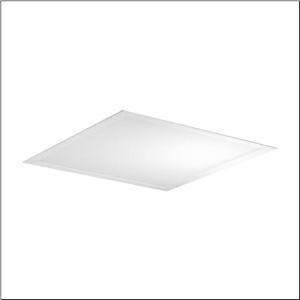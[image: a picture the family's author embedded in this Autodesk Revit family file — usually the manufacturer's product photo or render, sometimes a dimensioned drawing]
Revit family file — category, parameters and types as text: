
# Revit family: apollon_r__21_square_51mq11wd2454_78a7
name_source: partatom
category: Lighting Fixtures
units: mm (PartAtom-declared; Revit-internal decimal feet)

## family parameters
Cut with Voids When Loaded = No
Host = Face
Light Source = No
Part Type = Normal
Room Calculation Point = No
Round Connector Dimension = Use Diameter
Shared = No

## types (1)
- Apollon® 21 square (1 x LED, 4200 lm, 24.7 W, 4000K)
    Apparent Load = 25 VA
    CIE Flux Codes = 60 87 97 100 100
    Color Rendering = 80
    Color Temperature = 4000K
    Default Elevation = 1800 mm
    Description = Apollon® 21 square, office luminaire, primary optical cover: micro prismatic cover, of PMMA, CAT 2 (L<= 3000cd/m²), light emission: direct distribution, primary light characteristic: symmetric, installation type: lay-in mounting, LED, rated luminous flux: 4.200lm, luminous efficacy: 170lm/W, light colour: 840, colour temperature: 4000K, with terminal, 5-pole, mains connection: 220..240V, AC/DC, 0/50..60Hz, rated input power: 24.7W, housing, of aluminium, coated, traffic white (RAL 9016), module: M625, length: 620mm, width: 620mm, height: 30mm, housing upper side, of sheet steel, galvanised, protection rating (complete): IP20, protection rating (lamp compartment, on room side): IP54, insulation class (complete): insulation class II (safety insulation), certification: CE, ENEC, impact resistance: IK03, permissible operating ambient temperature: -20..+45°C, permissible storage temperature: -40..+80°C, packaging unit: 1 piece
    Height = 0 mm  [stored 0 ft]
    Lamp = 1 x LED
    Lamp Light Flux = 4200 lm
    Lamp Power = 24.7 W
    Lamp count = 1
    Length = 620 mm
    Luminous efficacy = 170 lm/W
    Manufacturer = Siteco
    ModVariant = No
    Model = 51MQ11WD2454
    Mounting Place = Ceiling
    Mounting Type = Recessed
    Number of Poles = 1
    OnlyDefault = Yes
    Power Factor = 1
    Product Name = Apollon® 21 square
    Product group = office luminaire | ceiling recessed
    ProductGroupID = 401
    Protection Class = Protection class II
    Protection Degree = IP 20
    RLX_Detail_Level = 1
    RLX_Emergency_Light_Flux = 0 lm
    RLX_Emergency_Type = 0
    RLX_Emergency_Type_DB = No
    RlxData = <blob elided: 12953 chars, md5=f17fdf0d>
    Socket = socket
    Standby Power = 0 W
    System Light Flux = 4200 lm
    System Power = 25 W
    Type Comments = Product without accessories
    Type Image = l_1291054.jpg
    URL = http://relux.com
    VarID = ---
    Voltage = 0 V
    Weight = 0.00 kg
    Width = 620 mm

note: [stored X ft] marks values corroborated as IEEE doubles in the binary element streams (Revit-internal decimal feet)

## geometry (parser evidence)
native form markers: Sweep x10
no freeform markers — native parametric forms only
